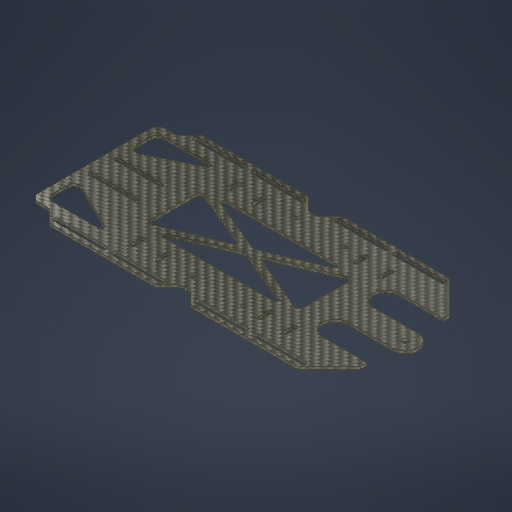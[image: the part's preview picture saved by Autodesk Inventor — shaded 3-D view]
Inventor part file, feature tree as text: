
AUTODESK INVENTOR PART (.ipt)
format: ipt  version: 2025 (Build 290162010, 162A)  size: 705,024 bytes
history: native  units: mm
features: extrude x7, sketch x7, fillet x1
ambient origin geometry x8: Origin, YZ Plane, XZ Plane, XY Plane, X Axis, Y Axis, Z Axis, Center Point
bodies: Solid1 (feature_tree)
feature tree (15):
  extrude  "Extrusion1"  Depth=73.0mm
  extrude  "Extrusion2"  Depth=58.0mm
  extrude  "Extrusion3"  Depth=50.0mm
  fillet  "Fillet1"  Radius=10.0mm
  extrude  "Extrusion4"  Depth=20.0mm
  extrude  "Extrusion5"  Depth=3.0mm
  extrude  "Extrusion6"  Depth=245.0mm
  extrude  "Extrusion7"  Depth=2.0mm TaperAngle=0.0deg
  sketch  "Sketch1"  dims[d0=220.0mm d1=73.0mm]
  sketch  "Sketch2"  dims[d2=190.0mm d3=58.0mm]
  sketch  "Sketch3"  dims[d4=5.0mm d5=50.0mm d6=10.0mm]
  sketch  "Sketch5"  dims[d7=20.0mm d8=7.5mm]
  sketch  "Sketch6"  dims[d9=3.0mm d10=7.5mm]
  sketch  "Sketch7"  dims[d11=3.0mm d12=245.0mm]
  sketch  "Sketch8"  dims[d13=100.0mm d14=2.0mm d15=0.0mm d16=80.0mm d17=20.0mm d18=7.5mm d19=3.0mm d20=7.5mm d21=3.0mm d22=10.0mm d23=10.0mm d24=35.0mm d25=3.0mm d26=35.0mm d27=3.0mm d28=55.5mm d29=55.0mm d30=4.0mm d31=37.5mm d32=3.5mm d36=30.0mm d37=15.0mm d38=10.0mm d39=10.0mm d40=5.0mm d41=2.0mm d42=0.0mm d43=45.0mm d44=45.0deg d45=45.0mm d46=45.0deg d49=1.0mm d50=0.0mm d51=6.0mm d52=20.0mm d53=35.0mm d54=35.0mm d55=20.0mm d56=20.0mm d57=35.0mm d58=20.0mm d59=35.0mm d60=20.0mm d61=15.0mm d62=40.0mm d63=80.0mm d64=3.5mm d65=3.5mm d66=3.5mm d67=3.5mm d68=1.0mm d69=0.0mm d70=25.0mm d71=4.7mm d72=1.0mm d73=0.0mm d76=120.0mm d77=50.0mm d78=2.5mm d79=2.5mm d80=2.5mm d81=2.5mm d82=3.0mm d83=2.0mm d84=5.0mm d85=3.0mm d86=0.0mm d87=50.0mm d88=25.0mm d89=50.0mm d90=25.0mm d91=5.0mm d92=5.0mm d93=2.0mm d94=3.0mm d95=0.0mm d47=0.5mm d48=0.872665mm d74=0.5mm d75=0.872665mm]
